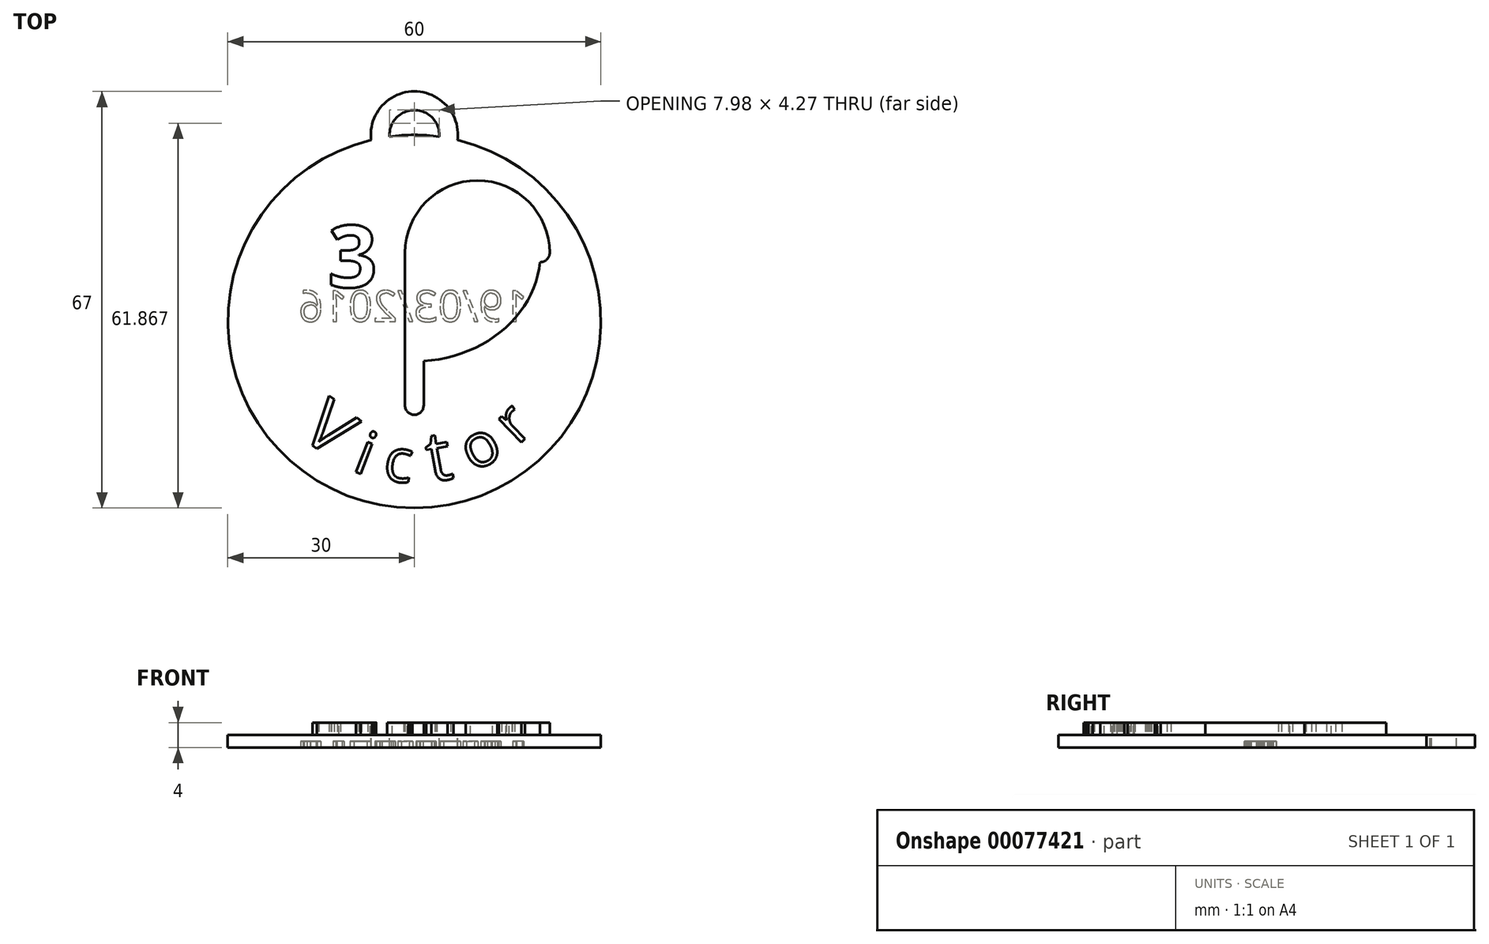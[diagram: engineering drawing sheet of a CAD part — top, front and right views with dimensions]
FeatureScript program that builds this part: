
annotation { "Feature Type Name" : "Feature", "Feature Type Description" : "" }
export const myFeature = defineFeature(function(context is Context, id is Id, definition is map)
    precondition{}
    {
        {
            var Q0;
            Q0=qCreatedBy(makeId("Top.planeOp"),FACE);
            var sketch = newSketch(context, id + "F0", { "sketchPlane" : qUnion([Q0])});
            skCircle(sketch, "E0", {"center": v(0, 0) * mm, "radius": 30 * mm});
            skSolve(sketch);
        }
        {
            var Q0;
            Q0=qSketchRegion(id+"F0",true);
            extrude(context, id + "F1", {"entities" : qUnion([Q0]), "oppositeDirection" : true, "depth" : 2 * mm});
        }
        {
            var Q0;
            Q0=qCreatedBy(makeId("Top.planeOp"),FACE);
            var sketch = newSketch(context, id + "F2", { "sketchPlane" : qUnion([Q0])});
            skEllipticalArc(sketch, "E1", {});
            skLineSegment(sketch, "E2", {"start": v(0, 0) * mm, "end": v(0, 30) * mm, "construction": true});
            skLineSegment(sketch, "E3", {"start": v(0, 11.04) * mm, "end": v(0, -13.5) * mm});
            skArc(sketch, "E4", {"start": v(20.27, 11.04) * mm, "mid": v(10.13, 21.17) * mm, "end": v(0, 11.04) * mm});
            skLineSegment(sketch, "E5", {"start": v(0, 11.04) * mm, "end": v(-16.84, 20.76) * mm, "construction": true});
            skLineSegment(sketch, "E6", {"start": v(0, 11.04) * mm, "end": v(-20.27, 11.04) * mm, "construction": true});
            skArc(sketch, "E7.0.startCap", {"start": v(-1.5, 11.04) * mm, "mid": v(0, 12.54) * mm, "end": v(1.5, 11.04) * mm});
            skArc(sketch, "E7.0.endCap", {"start": v(1.5, -13.5) * mm, "mid": v(0, -15) * mm, "end": v(-1.5, -13.5) * mm});
            skLineSegment(sketch, "E7.0.left", {"start": v(1.5, 11.04) * mm, "end": v(1.5, -13.5) * mm});
            skLineSegment(sketch, "E7.0.right", {"start": v(-1.5, 11.04) * mm, "end": v(-1.5, -13.5) * mm});
            skArc(sketch, "E8.0.startCap", {"start": v(21.77, 11.04) * mm, "mid": v(20.27, 9.54) * mm, "end": v(18.77, 11.04) * mm});
            skArc(sketch, "E8.0.endCap", {"start": v(1.5, 11.04) * mm, "mid": v(0, 9.54) * mm, "end": v(-1.5, 11.04) * mm});
            skArc(sketch, "E8.0.left", {"start": v(18.77, 11.04) * mm, "mid": v(10.13, 19.67) * mm, "end": v(1.5, 11.04) * mm});
            skArc(sketch, "E8.0.right", {"start": v(21.77, 11.04) * mm, "mid": v(10.13, 22.67) * mm, "end": v(-1.5, 11.04) * mm});
            skArc(sketch, "E8.1.startCap", {"start": v(-18.02, 21.68) * mm, "mid": v(-15.91, 21.95) * mm, "end": v(-15.65, 19.84) * mm});
            skArc(sketch, "E8.1.endCap", {"start": v(18.77, 11.04) * mm, "mid": v(20.27, 12.54) * mm, "end": v(21.77, 11.04) * mm});
            skFitSpline(sketch, "E8.1.left", {"points": [v(18.7, 9.5) * mm, v(18.8, 11.04) * mm, v(18.7, 12.6) * mm, v(18.36, 14.63) * mm, v(17.66, 16.6) * mm, v(16.63, 18.49) * mm, v(15.37, 20.3) * mm, v(13.44, 22.32) * mm, v(11.07, 24) * mm, v(8.94, 25.1) * mm, v(6.7, 26.01) * mm, v(4.32, 26.63) * mm, v(1.87, 26.95) * mm, v(0, 27.03) * mm, v(-1.87, 26.95) * mm, v(-4.32, 26.63) * mm, v(-6.7, 26.01) * mm, v(-8.94, 25.1) * mm, v(-11.07, 24) * mm, v(-13.44, 22.32) * mm, v(-15.37, 20.3) * mm, v(-16.63, 18.49) * mm, v(-17.66, 16.6) * mm, v(-18.36, 14.63) * mm, v(-18.7, 12.6) * mm, v(-18.8, 11.04) * mm, v(-18.7, 9.5) * mm, v(-18.36, 7.46) * mm, v(-17.66, 5.48) * mm, v(-16.63, 3.6) * mm, v(-15.37, 1.8) * mm, v(-13.44, -0.24) * mm, v(-11.07, -1.92) * mm, v(-8.94, -3.02) * mm, v(-6.7, -3.93) * mm, v(-4.32, -4.55) * mm, v(-1.87, -4.86) * mm, v(0, -4.94) * mm, v(1.87, -4.86) * mm, v(4.32, -4.55) * mm, v(6.7, -3.93) * mm, v(8.94, -3.02) * mm, v(11.07, -1.92) * mm, v(13.44, -0.24) * mm, v(15.37, 1.8) * mm, v(16.63, 3.6) * mm, v(17.66, 5.48) * mm, v(18.36, 7.46) * mm, v(18.7, 9.5) * mm, v(18.8, 11.04) * mm, v(18.7, 12.6) * mm]});
            skFitSpline(sketch, "E8.1.right", {"points": [v(21.7, 9.15) * mm, v(21.8, 11.04) * mm, v(21.7, 12.93) * mm, v(21.27, 15.42) * mm, v(20.42, 17.81) * mm, v(19.18, 20.07) * mm, v(17.69, 22.22) * mm, v(15.4, 24.61) * mm, v(12.65, 26.56) * mm, v(10.2, 27.83) * mm, v(7.62, 28.88) * mm, v(4.92, 29.58) * mm, v(2.12, 29.94) * mm, v(0, 30.03) * mm, v(-2.12, 29.94) * mm, v(-4.92, 29.58) * mm, v(-7.62, 28.88) * mm, v(-10.2, 27.83) * mm, v(-12.65, 26.56) * mm, v(-15.4, 24.61) * mm, v(-17.69, 22.22) * mm, v(-19.18, 20.07) * mm, v(-20.42, 17.81) * mm, v(-21.27, 15.42) * mm, v(-21.7, 12.93) * mm, v(-21.8, 11.04) * mm, v(-21.7, 9.15) * mm, v(-21.27, 6.67) * mm, v(-20.42, 4.27) * mm, v(-19.18, 2) * mm, v(-17.69, -0.14) * mm, v(-15.4, -2.53) * mm, v(-12.65, -4.48) * mm, v(-10.2, -5.75) * mm, v(-7.62, -6.8) * mm, v(-4.92, -7.5) * mm, v(-2.12, -7.86) * mm, v(0, -7.95) * mm, v(2.12, -7.86) * mm, v(4.92, -7.5) * mm, v(7.62, -6.8) * mm, v(10.2, -5.75) * mm, v(12.65, -4.48) * mm, v(15.4, -2.53) * mm, v(17.69, -0.14) * mm, v(19.18, 2) * mm, v(20.42, 4.27) * mm, v(21.27, 6.67) * mm, v(21.7, 9.15) * mm, v(21.8, 11.04) * mm, v(21.7, 12.93) * mm]});
            const initialGuessF2  = {"E1": [0, 0.011041626236194823, 1, 0, 0.020266667008310185, 0.017458373763805178, 2.5511335140588507, 0]};
            skSetInitialGuess(sketch, initialGuessF2);
            skSolve(sketch);
        }
        {
            var Q0;
            {var subQ0=sQuery(id+"F2.wireOp",EDGE,"E8.1.startCap");Q0=makeQuery(id+"F2.imprint","IMPRINT",FACE,{"disambiguationData":[TD([[makeQuery(id+"F2.imprint","IMPRINT",EDGE,{"derivedFrom":subQ0}),-1.0]])]});}
            var Q1;
            {var subQ0=sQuery(id+"F2.wireOp",EDGE,"E7.0.right");var subQ1=sQuery(id+"F2.wireOp",EDGE,"E1");var subQ2=makeQuery(id+"F2.imprint","INTERSECT",VERTEX,{"derivedFrom":[subQ1,subQ0]});Q1=makeQuery(id+"F2.imprint","IMPRINT",FACE,{"disambiguationData":[TD([[makeQuery(id+"F2.imprint","IMPRINT",EDGE,{"disambiguationData":[TD([[subQ2,-1.0]])],"derivedFrom":subQ1}),1.0]])]});}
            var Q2;
            {var subQ0=sQuery(id+"F2.wireOp",EDGE,"E3");var subQ1=sQuery(id+"F2.wireOp",EDGE,"E1");var subQ2=makeQuery(id+"F2.imprint","INTERSECT",VERTEX,{"derivedFrom":[subQ1,subQ0]});Q2=makeQuery(id+"F2.imprint","IMPRINT",FACE,{"disambiguationData":[TD([[makeQuery(id+"F2.imprint","IMPRINT",EDGE,{"disambiguationData":[TD([[subQ2,-1.0]])],"derivedFrom":subQ1}),1.0]])]});}
            var Q3;
            {var subQ0=sQuery(id+"F2.wireOp",EDGE,"E7.0.right");var subQ1=sQuery(id+"F2.wireOp",EDGE,"E1");var subQ2=makeQuery(id+"F2.imprint","INTERSECT",VERTEX,{"derivedFrom":[subQ1,subQ0]});Q3=makeQuery(id+"F2.imprint","IMPRINT",FACE,{"disambiguationData":[TD([[makeQuery(id+"F2.imprint","IMPRINT",EDGE,{"disambiguationData":[TD([[subQ2,-1.0]])],"derivedFrom":subQ1}),-1.0]])]});}
            var Q4;
            {var subQ0=sQuery(id+"F2.wireOp",EDGE,"E3");var subQ1=sQuery(id+"F2.wireOp",EDGE,"E1");var subQ2=makeQuery(id+"F2.imprint","INTERSECT",VERTEX,{"derivedFrom":[subQ1,subQ0]});Q4=makeQuery(id+"F2.imprint","IMPRINT",FACE,{"disambiguationData":[TD([[makeQuery(id+"F2.imprint","IMPRINT",EDGE,{"disambiguationData":[TD([[subQ2,-1.0]])],"derivedFrom":subQ1}),-1.0]])]});}
            var Q5;
            {var subQ0=sQuery(id+"F2.wireOp",EDGE,"E7.0.left");var subQ1=sQuery(id+"F2.wireOp",EDGE,"E1");var subQ2=makeQuery(id+"F2.imprint","INTERSECT",VERTEX,{"derivedFrom":[subQ1,subQ0]});Q5=makeQuery(id+"F2.imprint","IMPRINT",FACE,{"disambiguationData":[TD([[makeQuery(id+"F2.imprint","IMPRINT",EDGE,{"disambiguationData":[TD([[subQ2,-1.0]])],"derivedFrom":subQ1}),-1.0]])]});}
            var Q6;
            {var subQ0=sQuery(id+"F2.wireOp",EDGE,"E7.0.left");var subQ1=sQuery(id+"F2.wireOp",EDGE,"E1");var subQ2=makeQuery(id+"F2.imprint","INTERSECT",VERTEX,{"derivedFrom":[subQ1,subQ0]});Q6=makeQuery(id+"F2.imprint","IMPRINT",FACE,{"disambiguationData":[TD([[makeQuery(id+"F2.imprint","IMPRINT",EDGE,{"disambiguationData":[TD([[subQ2,-1.0]])],"derivedFrom":subQ1}),1.0]])]});}
            var Q7;
            {var subQ0=sQuery(id+"F2.wireOp",EDGE,"E4");var subQ1=sQuery(id+"F2.wireOp",EDGE,"E1");var subQ2=makeQuery(id+"F2.imprint","INTERSECT",VERTEX,{"derivedFrom":[subQ1,subQ0]});Q7=makeQuery(id+"F2.imprint","IMPRINT",FACE,{"disambiguationData":[TD([[makeQuery(id+"F2.imprint","IMPRINT",EDGE,{"disambiguationData":[TD([[subQ2,1.0]])],"derivedFrom":subQ1}),-1.0]])]});}
            var Q8;
            {var subQ0=sQuery(id+"F2.wireOp",EDGE,"E4");var subQ1=sQuery(id+"F2.wireOp",EDGE,"E1");var subQ2=makeQuery(id+"F2.imprint","INTERSECT",VERTEX,{"derivedFrom":[subQ1,subQ0]});Q8=makeQuery(id+"F2.imprint","IMPRINT",FACE,{"disambiguationData":[TD([[makeQuery(id+"F2.imprint","IMPRINT",EDGE,{"disambiguationData":[TD([[subQ2,1.0]])],"derivedFrom":subQ1}),1.0]])]});}
            var Q9;
            {var subQ5=sQuery(id+"F2.wireOp",EDGE,"E8.0.left");Q9=makeQuery(id+"F2.imprint","IMPRINT",FACE,{"disambiguationData":[TD([[makeQuery(id+"F2.imprint","IMPRINT",EDGE,{"derivedFrom":subQ5}),-1.0]])]});}
            var Q10;
            {var subQ5=sQuery(id+"F2.wireOp",EDGE,"E8.0.right");Q10=makeQuery(id+"F2.imprint","IMPRINT",FACE,{"disambiguationData":[TD([[makeQuery(id+"F2.imprint","IMPRINT",EDGE,{"derivedFrom":subQ5}),1.0]])]});}
            var Q11;
            {var subQ0=sQuery(id+"F2.wireOp",EDGE,"E4");var subQ1=sQuery(id+"F2.wireOp",EDGE,"E3");var subQ2=makeQuery(id+"F2.imprint","INTERSECT",VERTEX,{"derivedFrom":[subQ1,subQ0]});Q11=makeQuery(id+"F2.imprint","IMPRINT",FACE,{"disambiguationData":[TD([[makeQuery(id+"F2.imprint","IMPRINT",EDGE,{"disambiguationData":[TD([[subQ2,-1.0]])],"derivedFrom":subQ1}),-1.0]])]});}
            var Q12;
            {var subQ0=sQuery(id+"F2.wireOp",EDGE,"E4");var subQ1=sQuery(id+"F2.wireOp",EDGE,"E3");var subQ2=makeQuery(id+"F2.imprint","INTERSECT",VERTEX,{"derivedFrom":[subQ1,subQ0]});Q12=makeQuery(id+"F2.imprint","IMPRINT",FACE,{"disambiguationData":[TD([[makeQuery(id+"F2.imprint","IMPRINT",EDGE,{"disambiguationData":[TD([[subQ2,-1.0]])],"derivedFrom":subQ1}),1.0]])]});}
            var Q13;
            {var subQ0=sQuery(id+"F2.wireOp",EDGE,"E8.0.endCap");var subQ1=sQuery(id+"F2.wireOp",EDGE,"E3");var subQ2=makeQuery(id+"F2.imprint","INTERSECT",VERTEX,{"derivedFrom":[subQ1,subQ0]});Q13=makeQuery(id+"F2.imprint","IMPRINT",FACE,{"disambiguationData":[TD([[makeQuery(id+"F2.imprint","IMPRINT",EDGE,{"disambiguationData":[TD([[subQ2,-1.0]])],"derivedFrom":subQ1}),-1.0]])]});}
            var Q14;
            {var subQ0=sQuery(id+"F2.wireOp",EDGE,"E8.0.endCap");var subQ1=sQuery(id+"F2.wireOp",EDGE,"E3");var subQ2=makeQuery(id+"F2.imprint","INTERSECT",VERTEX,{"derivedFrom":[subQ1,subQ0]});Q14=makeQuery(id+"F2.imprint","IMPRINT",FACE,{"disambiguationData":[TD([[makeQuery(id+"F2.imprint","IMPRINT",EDGE,{"disambiguationData":[TD([[subQ2,-1.0]])],"derivedFrom":subQ1}),1.0]])]});}
            var Q15;
            {var subQ1=sQuery(id+"F2.wireOp",EDGE,"E7.0.endCap");Q15=makeQuery(id+"F2.imprint","IMPRINT",FACE,{"disambiguationData":[TD([[makeQuery(id+"F2.imprint","IMPRINT",EDGE,{"derivedFrom":subQ1}),-1.0]])]});}
            extrude(context, id + "F3", {"entities" : qUnion([Q0, Q1, Q2, Q3, Q4, Q5, Q6, Q7, Q8, Q9, Q10, Q11, Q12, Q13, Q14, Q15]), "operationType" : NewBodyOperationType.ADD, "depth" : 2 * mm});
        }
        {
            var Q0;
            Q0=qCreatedBy(makeId("Top.planeOp"),FACE);
            var sketch = newSketch(context, id + "F4", { "sketchPlane" : qUnion([Q0])});
            skText(sketch, "E9", { "text": "3", "fontName": "OpenSans-Bold.ttf"});
            skText(sketch, "E10", { "text": "D", "fontName": "OpenSans-Bold.ttf"});
            const initialGuessF4  = {"E9": [-0.0139, 0.0055, 1, 0, 0.01], "E10": [0.0055, 0.0055, 1, 0, 0.01]};
            skSetInitialGuess(sketch, initialGuessF4);
            skSolve(sketch);
        }
        {
            var Q0;
            Q0=qSketchRegion(id+"F4",true);
            extrude(context, id + "F5", {"entities" : qUnion([Q0]), "operationType" : NewBodyOperationType.ADD, "depth" : 2 * mm});
        }
        {
            var Q0;
            {var subQ8=sQuery(id+"F0.wireOp",EDGE,"E0");Q0=makeQuery(id+"F3.boolean.opBoolean","SPLIT",FACE,{"disambiguationData":[TD([makeQuery(id+"F1.opExtrude","SWEPT_FACE",FACE,{"disambiguationData":[OSD([subQ8])]})])],"derivedFrom":makeQuery(id+"F1.opExtrude","CAP_FACE",FACE,{"disambiguationData":[OSD([subQ8])],"isStart":true})});}
            var sketch = newSketch(context, id + "F6", { "sketchPlane" : qUnion([Q0])});
            skCircle(sketch, "E11.0", {"center": v(0, 0) * mm, "radius": 26 * mm, "construction": true});
            skText(sketch, "E12", { "text": "V", "fontName": "OpenSans-Regular.ttf"});
            skText(sketch, "E13", { "text": "i", "fontName": "OpenSans-Regular.ttf"});
            skText(sketch, "E14", { "text": "c", "fontName": "OpenSans-Regular.ttf"});
            skText(sketch, "E15", { "text": "t", "fontName": "OpenSans-Regular.ttf"});
            skText(sketch, "E16", { "text": "o", "fontName": "OpenSans-Regular.ttf"});
            skText(sketch, "E17", { "text": "r", "fontName": "OpenSans-Regular.ttf"});
            const initialGuessF6  = {"E12": [-0.01861, -0.01815, 0.7836, -0.62126, 0.008], "E13": [-0.01017, -0.02393, 0.93265, -0.36077, 0.007], "E14": [-0.00517, -0.02548, 0.99312, -0.11707, 0.007], "E15": [0.00265, -0.02586, 0.98507, 0.17213, 0.008], "E16": [0.00936, -0.02426, 0.89116, 0.4537, 0.007], "E17": [0.0166, -0.02, 0.72025, 0.69372, 0.007]};
            skSetInitialGuess(sketch, initialGuessF6);
            skSolve(sketch);
        }
        {
            var Q0;
            Q0=qSketchRegion(id+"F6",true);
            extrude(context, id + "F7", {"entities" : qUnion([Q0]), "operationType" : NewBodyOperationType.ADD, "depth" : 2 * mm});
        }
        {
            var Q0;
            Q0=qCreatedBy(makeId("Top.planeOp"),FACE);
            var sketch = newSketch(context, id + "F8", { "sketchPlane" : qUnion([Q0])});
            skArc(sketch, "E18", {"start": v(5.48, 29.5) * mm, "mid": v(0, 35.5) * mm, "end": v(-5.48, 29.5) * mm});
            skArc(sketch, "E19.0.startCap", {"start": v(6.97, 29.36) * mm, "mid": v(5.34, 28) * mm, "end": v(3.98, 29.63) * mm});
            skArc(sketch, "E19.0.endCap", {"start": v(-3.98, 29.63) * mm, "mid": v(-5.34, 28) * mm, "end": v(-6.97, 29.36) * mm});
            skArc(sketch, "E19.0.left", {"start": v(3.98, 29.63) * mm, "mid": v(0, 34) * mm, "end": v(-3.98, 29.63) * mm});
            skArc(sketch, "E19.0.right", {"start": v(6.97, 29.36) * mm, "mid": v(0, 37) * mm, "end": v(-6.97, 29.36) * mm});
            skSolve(sketch);
        }
        {
            var Q0;
            Q0=qSketchRegion(id+"F8",true);
            extrude(context, id + "F9", {"entities" : qUnion([Q0]), "operationType" : NewBodyOperationType.ADD, "oppositeDirection" : true, "depth" : 2 * mm});
        }
        {
            var Q0;
            Q0=makeQuery(id+"F9.boolean.opBoolean","MERGE",FACE,{"derivedFrom":[makeQuery(id+"F1.opExtrude","CAP_FACE",FACE,{"disambiguationData":[OSD([sQuery(id+"F0.wireOp",EDGE,"E0")])],"isStart":false}),makeQuery(id+"F9.opExtrude","CAP_FACE",FACE,{"disambiguationData":[OSD([sQuery(id+"F8.wireOp",EDGE,"E19.0.startCap"),sQuery(id+"F8.wireOp",EDGE,"E19.0.endCap"),sQuery(id+"F8.wireOp",EDGE,"E19.0.left"),sQuery(id+"F8.wireOp",EDGE,"E19.0.right")])],"isStart":false})]});
            var sketch = newSketch(context, id + "F10", { "sketchPlane" : qUnion([Q0])});
            skText(sketch, "E20", { "text": "19/03/2016", "fontName": "OpenSans-Regular.ttf"});
            const initialGuessF10  = {"E20": [0.01826, 0, -1, 0, 0.005]};
            skSetInitialGuess(sketch, initialGuessF10);
            skSolve(sketch);
        }
        {
            var Q0;
            Q0=qSketchRegion(id+"F10",true);
            extrude(context, id + "F11", {"entities" : qUnion([Q0]), "operationType" : NewBodyOperationType.REMOVE, "oppositeDirection" : true, "depth" : 1 * mm});
        }
    });
